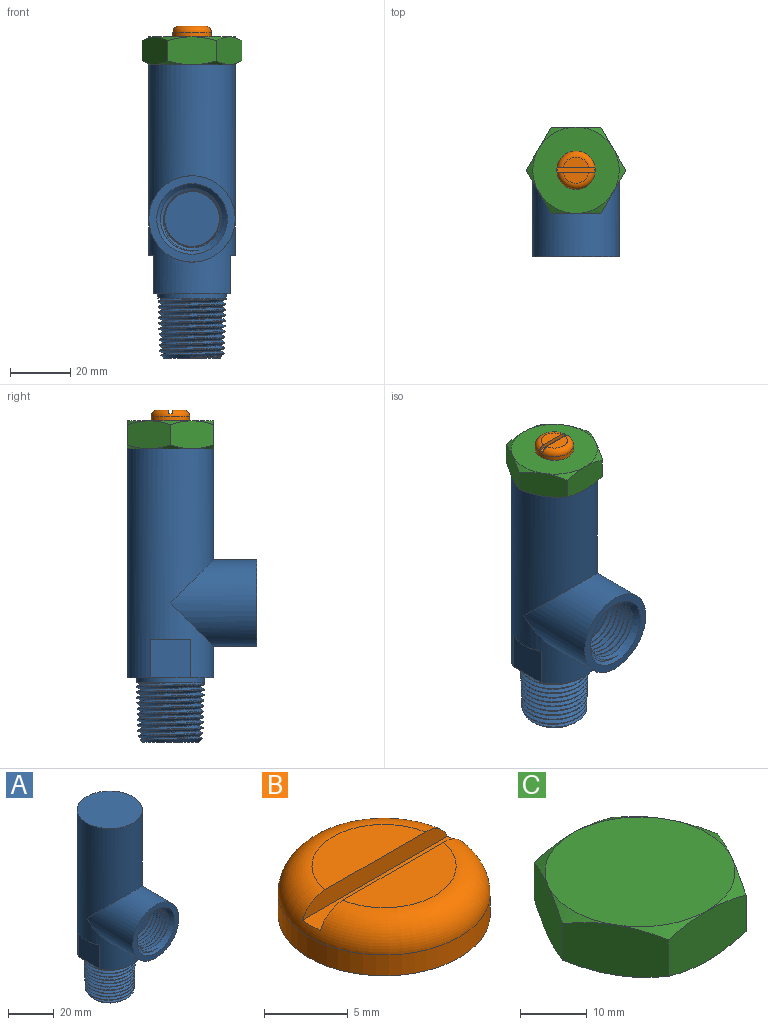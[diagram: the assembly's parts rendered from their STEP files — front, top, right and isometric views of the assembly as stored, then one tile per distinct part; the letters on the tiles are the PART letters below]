
ASSEMBLY  parts=3 mates=2
PART A: 33 faces, bbox 28.6x42.9x97.7 mm
  f0: plane 28.58x25.4mm, normal (0,0,-1), area 209.6mm2, adj f1,f6,f8,f9
  f1: cylinder r=14.29mm len=75.76mm, axis (0,0,-1), area 5638.7mm2, adj f0,f2,f3,f5,f6,f7,f8
  f2: plane 28.58x28.58mm, normal (0,0,1), area 641.3mm2, adj f1
  f3: cylinder r=14.29mm len=28.58mm, axis (0,1,0), area 1748.7mm2, adj f1,f4
  f4: plane 28.58x28.58mm, normal (0,-1,0), area 212.4mm2, adj f3,f32
  f5: plane 13.09x1.59mm, normal (0,0,-1), area 14mm2, adj f1,f6
  f6: plane 13.09x12.7mm, normal (-1,0,0), area 166.3mm2, adj f0,f1,f5
  f7: plane 13.09x1.59mm, normal (0,0,-1), area 14mm2, adj f1,f8
  f8: plane 13.09x12.7mm, normal (1,0,0), area 166.3mm2, adj f0,f1,f7
  f9: cone r=11.29mm half-angle=1.8deg, axis (0,0,1), area 112.4mm2, adj f0,f10,f20,f25,f26
  f10: cone r=11.29mm half-angle=1.8deg, axis (0,0,1), area 18mm2, adj f9,f11,f25,f26
  f11: cone r=11.29mm half-angle=1.8deg, axis (0,0,1), area 17.9mm2, adj f10,f12,f25,f26
  f12: cone r=11.29mm half-angle=1.8deg, axis (0,0,1), area 17.8mm2, adj f11,f13,f25,f26
  f13: cone r=11.29mm half-angle=1.8deg, axis (0,0,1), area 17.7mm2, adj f12,f14,f25,f26
  f14: cone r=11.29mm half-angle=1.8deg, axis (0,0,1), area 17.6mm2, adj f13,f15,f25,f26
  f15: cone r=11.29mm half-angle=1.8deg, axis (0,0,1), area 17.5mm2, adj f14,f16,f25,f26
  f16: cone r=11.29mm half-angle=1.8deg, axis (0,0,1), area 17.5mm2, adj f15,f17,f25,f26
  f17: cone r=11.29mm half-angle=1.8deg, axis (0,0,1), area 17.4mm2, adj f16,f18,f25,f26
  f18: cone r=11.29mm half-angle=1.8deg, axis (0,0,1), area 17.3mm2, adj f17,f19,f25,f26
  f19: cone r=11.29mm half-angle=1.8deg, axis (0,0,1), area 13.7mm2, adj f18,f22,f25,f26
  f20: plane 22.6x22.6mm, normal (0,0,-1), area 38.7mm2, adj f9,f24,f25,f26
  f21: cone r=10.71mm half-angle=45deg, axis (0,0,1), area 57.9mm2, adj f22,f23,f24,f25,f26
  f22: cone r=10.71mm half-angle=45deg, axis (0,0,1), area 13.5mm2, adj f19,f21,f25,f26
  f23: plane 18.61x18.61mm, normal (0,0,-1), area 272.1mm2, adj f21
  f24: bspline ~20.35x20.28mm, area 151.6mm2, adj f20,f21,f25,f26
  f25: bspline ~22.89x22.86mm, area 934.1mm2, adj f9,f10,f11,f12,f13,f14,f15,f16
  f26: bspline ~22.87x22.84mm, area 895.7mm2, adj f9,f10,f11,f12,f13,f14,f15,f16
  f27: cone r=10.67mm half-angle=1.8deg, axis (0,-1,0), area 90.6mm2, adj f28,f30,f31,f32
  f28: plane 19.34x19.31mm, normal (0,-1,0), area 292.1mm2, adj f27,f29,f30,f31
  f29: bspline ~18.79x18.77mm, area 81.5mm2, adj f28,f30,f31,f32
  f30: bspline ~21.53x21.5mm, area 551.1mm2, adj f27,f28,f29,f32
  f31: bspline ~21.58x21.52mm, area 574.8mm2, adj f27,f28,f29,f32
  f32: cone r=11.68mm half-angle=45deg, axis (0,-1,0), area 161mm2, adj f4,f27,f29,f30,f31
PART B: 8 faces, bbox 13.7x13.7x3.6 mm
  f0: plane 8.5x3.56mm, normal (0,0,1), area 22.7mm2, adj f4,f5
  f1: cylinder r=6.35mm len=12.7mm, axis (0,0,-1), area 60.8mm2, adj f3,f4
  f2: plane 8.5x3.56mm, normal (0,0,1), area 22.7mm2, adj f4,f6
  f3: plane 12.7x12.7mm, normal (0,0,-1), area 126.7mm2, adj f1
  f4: torus R=4.32mm, axis (0,0,1), area 105.2mm2, adj f0,f1,f2,f5,f6,f7
  f5: plane 12.31x1.27mm, normal (0,1,0), area 14.3mm2, adj f0,f4,f7
  f6: plane 12.31x1.27mm, normal (0,-1,0), area 14.3mm2, adj f2,f4,f7
  f7: plane 12.4x1.52mm, normal (0,0,1), area 18.9mm2, adj f4,f5,f6
PART C: 20 faces, bbox 33x33x9.3 mm
  f0: plane 14.29x9.28mm, normal (-0.87,-0.5,0), area 138.5mm2, adj f1,f5,f6,f7,f17,f18
  f1: plane 16.51x9.27mm, normal (0,-1,0), area 138.5mm2, adj f0,f2,f6,f11,f13,f18
  f2: plane 14.29x9.28mm, normal (0.87,-0.5,0), area 138.5mm2, adj f1,f3,f10,f11,f13,f14
  f3: plane 14.29x9.28mm, normal (0.87,0.5,0), area 138.5mm2, adj f2,f4,f9,f10,f14,f15
  f4: plane 16.51x9.27mm, normal (0,1,0), area 138.5mm2, adj f3,f5,f8,f9,f15,f16
  f5: plane 14.29x9.28mm, normal (-0.87,0.5,0), area 138.5mm2, adj f0,f4,f7,f8,f16,f17
  f6: cone r=14.29mm half-angle=60deg, axis (0,0,-1), area 12.7mm2, adj f0,f1,f12
  f7: cone r=14.29mm half-angle=60deg, axis (0,0,-1), area 12.7mm2, adj f0,f5,f12
  f8: cone r=14.29mm half-angle=60deg, axis (0,0,-1), area 12.7mm2, adj f4,f5,f12
  f9: cone r=14.29mm half-angle=60deg, axis (0,0,-1), area 12.7mm2, adj f3,f4,f12
  f10: cone r=14.29mm half-angle=60deg, axis (0,0,-1), area 12.7mm2, adj f2,f3,f12
  f11: cone r=14.29mm half-angle=60deg, axis (0,0,-1), area 12.7mm2, adj f1,f2,f12
  f12: plane 28.58x28.58mm, normal (0,0,1), area 641.3mm2, adj f6,f7,f8,f9,f10,f11
  f13: cone r=14.29mm half-angle=60deg, axis (0,0,1), area 12.7mm2, adj f1,f2,f19
  f14: cone r=14.29mm half-angle=60deg, axis (0,0,1), area 12.7mm2, adj f2,f3,f19
  f15: cone r=14.29mm half-angle=60deg, axis (0,0,1), area 12.7mm2, adj f3,f4,f19
  f16: cone r=14.29mm half-angle=60deg, axis (0,0,1), area 12.7mm2, adj f4,f5,f19
  f17: cone r=14.29mm half-angle=60deg, axis (0,0,1), area 12.7mm2, adj f0,f5,f19
  f18: cone r=14.29mm half-angle=60deg, axis (0,0,1), area 12.7mm2, adj f0,f1,f19
  f19: plane 28.58x28.58mm, normal (0,0,-1), area 641.3mm2, adj f13,f14,f15,f16,f17,f18
PLACE A t=(-60.37,-2.6,-17.07)mm
PLACE B t=(-60.37,-2.6,-17.07)mm
PLACE C t=(-60.37,-2.6,-17.07)mm
MATE fastened B.f1 <-> C.f6  axis (0,0,-1) through (-60.37,-2.6,89.29)mm
MATE fastened C.f6 <-> A.f1  axis (0,0,-1) through (-60.37,-2.6,80.02)mm
